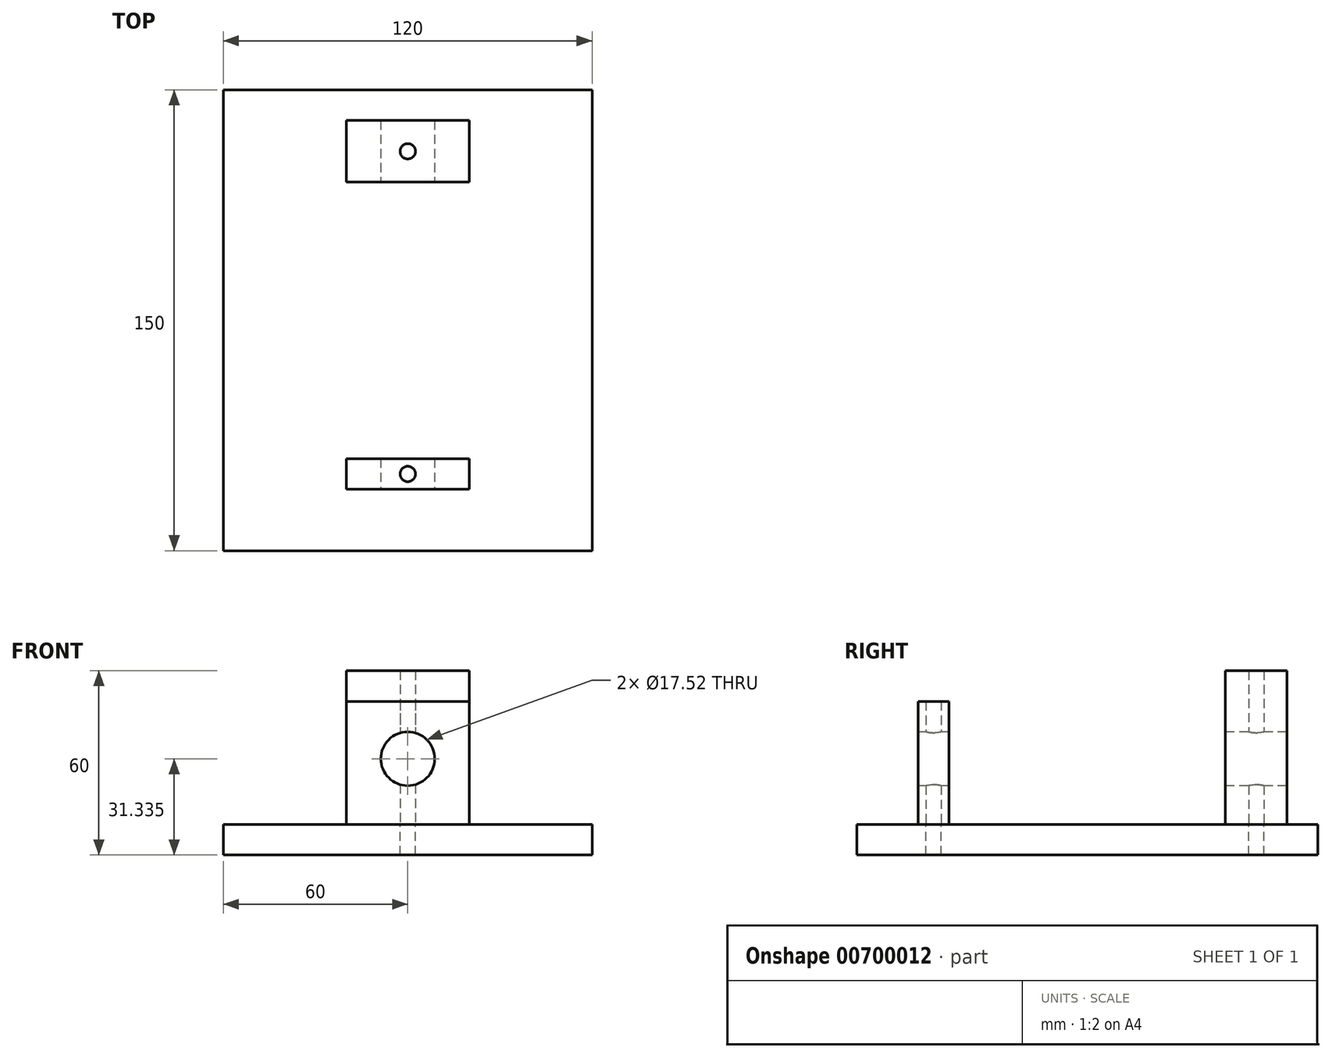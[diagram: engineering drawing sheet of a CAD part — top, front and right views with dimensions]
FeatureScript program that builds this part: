
annotation { "Feature Type Name" : "Feature", "Feature Type Description" : "" }
export const myFeature = defineFeature(function(context is Context, id is Id, definition is map)
    precondition{}
    {
        {
            var Q0;
            Q0=qCreatedBy(makeId("Top.planeOp"),FACE);
            var sketch = newSketch(context, id + "F0", { "sketchPlane" : qUnion([Q0])});
            skLineSegment(sketch, "E0.bottom", {"start": v(-60, 75) * mm, "end": v(60, 75) * mm});
            skLineSegment(sketch, "E0.top", {"start": v(-60, -75) * mm, "end": v(60, -75) * mm});
            skLineSegment(sketch, "E0.left", {"start": v(-60, 75) * mm, "end": v(-60, -75) * mm});
            skLineSegment(sketch, "E0.right", {"start": v(60, 75) * mm, "end": v(60, -75) * mm});
            skLineSegment(sketch, "E1.bottom", {"start": v(-20, -45) * mm, "end": v(20, -45) * mm});
            skLineSegment(sketch, "E1.top", {"start": v(-20, -55) * mm, "end": v(20, -55) * mm});
            skLineSegment(sketch, "E1.left", {"start": v(-20, -45) * mm, "end": v(-20, -55) * mm});
            skLineSegment(sketch, "E1.right", {"start": v(20, -45) * mm, "end": v(20, -55) * mm});
            skLineSegment(sketch, "E2.bottom", {"start": v(-20, 45) * mm, "end": v(20, 45) * mm});
            skLineSegment(sketch, "E2.top", {"start": v(-20, 65) * mm, "end": v(20, 65) * mm});
            skLineSegment(sketch, "E2.left", {"start": v(-20, 65) * mm, "end": v(-20, 45) * mm});
            skLineSegment(sketch, "E2.right", {"start": v(20, 65) * mm, "end": v(20, 45) * mm});
            skCircle(sketch, "E3", {"center": v(0, 55) * mm, "radius": 2.5 * mm});
            skCircle(sketch, "E4", {"center": v(0, -50) * mm, "radius": 2.5 * mm});
            skLineSegment(sketch, "E5", {"start": v(0, 75) * mm, "end": v(0, -75) * mm, "construction": true});
            skLineSegment(sketch, "E6", {"start": v(-60, 0) * mm, "end": v(60, 0) * mm, "construction": true});
            skSolve(sketch);
        }
        {
            var Q0;
            Q0=makeQuery(id+"F0.imprint","IMPRINT",FACE,{"disambiguationData":[TD([[makeQuery(id+"F0.imprint","IMPRINT",EDGE,{"derivedFrom":sQuery(id+"F0.wireOp",EDGE,"E0.bottom")}),-1.0]])]});
            var Q1;
            Q1=makeQuery(id+"F0.imprint","IMPRINT",FACE,{"disambiguationData":[TD([[makeQuery(id+"F0.imprint","IMPRINT",EDGE,{"derivedFrom":sQuery(id+"F0.wireOp",EDGE,"E2.bottom")}),1.0]])]});
            var Q2;
            Q2=makeQuery(id+"F0.imprint","IMPRINT",FACE,{"disambiguationData":[TD([[makeQuery(id+"F0.imprint","IMPRINT",EDGE,{"derivedFrom":sQuery(id+"F0.wireOp",EDGE,"E1.bottom")}),-1.0]])]});
            var Q3;
            Q3=makeQuery(id+"F0.imprint","IMPRINT",FACE,{"disambiguationData":[TD([[makeQuery(id+"F0.imprint","IMPRINT",EDGE,{"derivedFrom":sQuery(id+"F0.wireOp",EDGE,"E3")}),1.0]])]});
            var Q4;
            Q4=makeQuery(id+"F0.imprint","IMPRINT",FACE,{"disambiguationData":[TD([[makeQuery(id+"F0.imprint","IMPRINT",EDGE,{"derivedFrom":sQuery(id+"F0.wireOp",EDGE,"E4")}),1.0]])]});
            extrude(context, id + "F1", {"entities" : qUnion([Q0, Q1, Q2, Q3, Q4]), "oppositeDirection" : true, "depth" : 10 * mm, "offsetDistance" : 25 * mm});
        }
        {
            var Q0;
            Q0=makeQuery(id+"F0.imprint","IMPRINT",FACE,{"disambiguationData":[TD([[makeQuery(id+"F0.imprint","IMPRINT",EDGE,{"derivedFrom":sQuery(id+"F0.wireOp",EDGE,"E2.bottom")}),1.0]])]});
            extrude(context, id + "F2", {"entities" : qUnion([Q0]), "depth" : 50 * mm, "offsetDistance" : 25 * mm});
        }
        {
            var Q0;
            Q0=makeQuery(id+"F0.imprint","IMPRINT",FACE,{"disambiguationData":[TD([[makeQuery(id+"F0.imprint","IMPRINT",EDGE,{"derivedFrom":sQuery(id+"F0.wireOp",EDGE,"E3")}),1.0]])]});
            extrude(context, id + "F3", {"entities" : qUnion([Q0]), "operationType" : NewBodyOperationType.REMOVE, "oppositeDirection" : true, "depth" : 25 * mm, "offsetDistance" : 25 * mm});
        }
        {
            var Q0;
            Q0=makeQuery(id+"F0.imprint","IMPRINT",FACE,{"disambiguationData":[TD([[makeQuery(id+"F0.imprint","IMPRINT",EDGE,{"derivedFrom":sQuery(id+"F0.wireOp",EDGE,"E4")}),1.0]])]});
            extrude(context, id + "F4", {"entities" : qUnion([Q0]), "operationType" : NewBodyOperationType.REMOVE, "oppositeDirection" : true, "depth" : 25 * mm, "offsetDistance" : 25 * mm});
        }
        {
            var Q0;
            Q0=makeQuery(id+"F0.imprint","IMPRINT",FACE,{"disambiguationData":[TD([[makeQuery(id+"F0.imprint","IMPRINT",EDGE,{"derivedFrom":sQuery(id+"F0.wireOp",EDGE,"E1.bottom")}),-1.0]])]});
            extrude(context, id + "F5", {"entities" : qUnion([Q0]), "depth" : 40 * mm, "offsetDistance" : 25 * mm});
        }
        {
            var Q0;
            Q0=qCreatedBy(makeId("Front.planeOp"),FACE);
            var sketch = newSketch(context, id + "F6", { "sketchPlane" : qUnion([Q0])});
            skCircle(sketch, "E7", {"center": v(0, 21.33) * mm, "radius": 8.76 * mm});
            skSolve(sketch);
        }
        {
            var Q0;
            Q0=makeQuery(id+"F6.imprint","IMPRINT",FACE,{"disambiguationData":[TD([[makeQuery(id+"F6.imprint","IMPRINT",EDGE,{"derivedFrom":sQuery(id+"F6.wireOp",EDGE,"E7")}),1.0]])]});
            extrude(context, id + "F7", {"entities" : qUnion([Q0]), "operationType" : NewBodyOperationType.REMOVE, "endBound" : BoundingType.SYMMETRIC, "oppositeDirection" : true, "depth" : 160 * mm, "offsetDistance" : 25 * mm});
        }
        {
            var Q0;
            Q0=makeQuery(id+"F6.imprint","IMPRINT",FACE,{"disambiguationData":[TD([[makeQuery(id+"F6.imprint","IMPRINT",EDGE,{"derivedFrom":sQuery(id+"F6.wireOp",EDGE,"E7")}),1.0]])]});
            extrude(context, id + "F8", {"entities" : qUnion([Q0]), "operationType" : NewBodyOperationType.REMOVE, "depth" : 68.3 * mm, "offsetDistance" : 25 * mm});
        }
    });
